# Revit family: Accessory-Sink_Rack-KOHLER-K-33714_1
name_source: partatom
category: Specialty Equipment
units: mm (PartAtom-declared; Revit-internal decimal feet)

## family parameters
Cut with Voids When Loaded = No
Host = Face
OmniClass Number = 23.31.25.00
OmniClass Title = Toilet and Bath Specialties
Part Type = Normal
Room Calculation Point = No
Round Connector Dimension = Use Diameter
Shared = No

## types (1)
- ST-Stainless Steel
    ADA Compliant = No
    Assembly Code = C1030200
    Date Modified = 08/09/2023
    Default Elevation = 42"
    Description = 33 Single Bowl Basin Rack
    Finish = KOHLER-Metal-ST-Stainless_Steel
    Height = 1 13/16"
    Length = 29"
    Manufacturer = Kohler Co.
    Master Format 2014 = 10 28 00
    Master Format 2014 Name = Toilet, Bath, and Laundry Accessories
    Material = Stainless Steel
    Model = K-33714-ST
    Product Documentation Link = https://www.us.kohler.com
    Product Page URL = http://www.us.kohler.com
    Type = 1
    URL = https://www.us.kohler.com
    WaterSense Certified = No
    Width = 14 5/16"

## geometry (parser evidence)
native form markers: Sweep x5
no freeform markers — native parametric forms only
